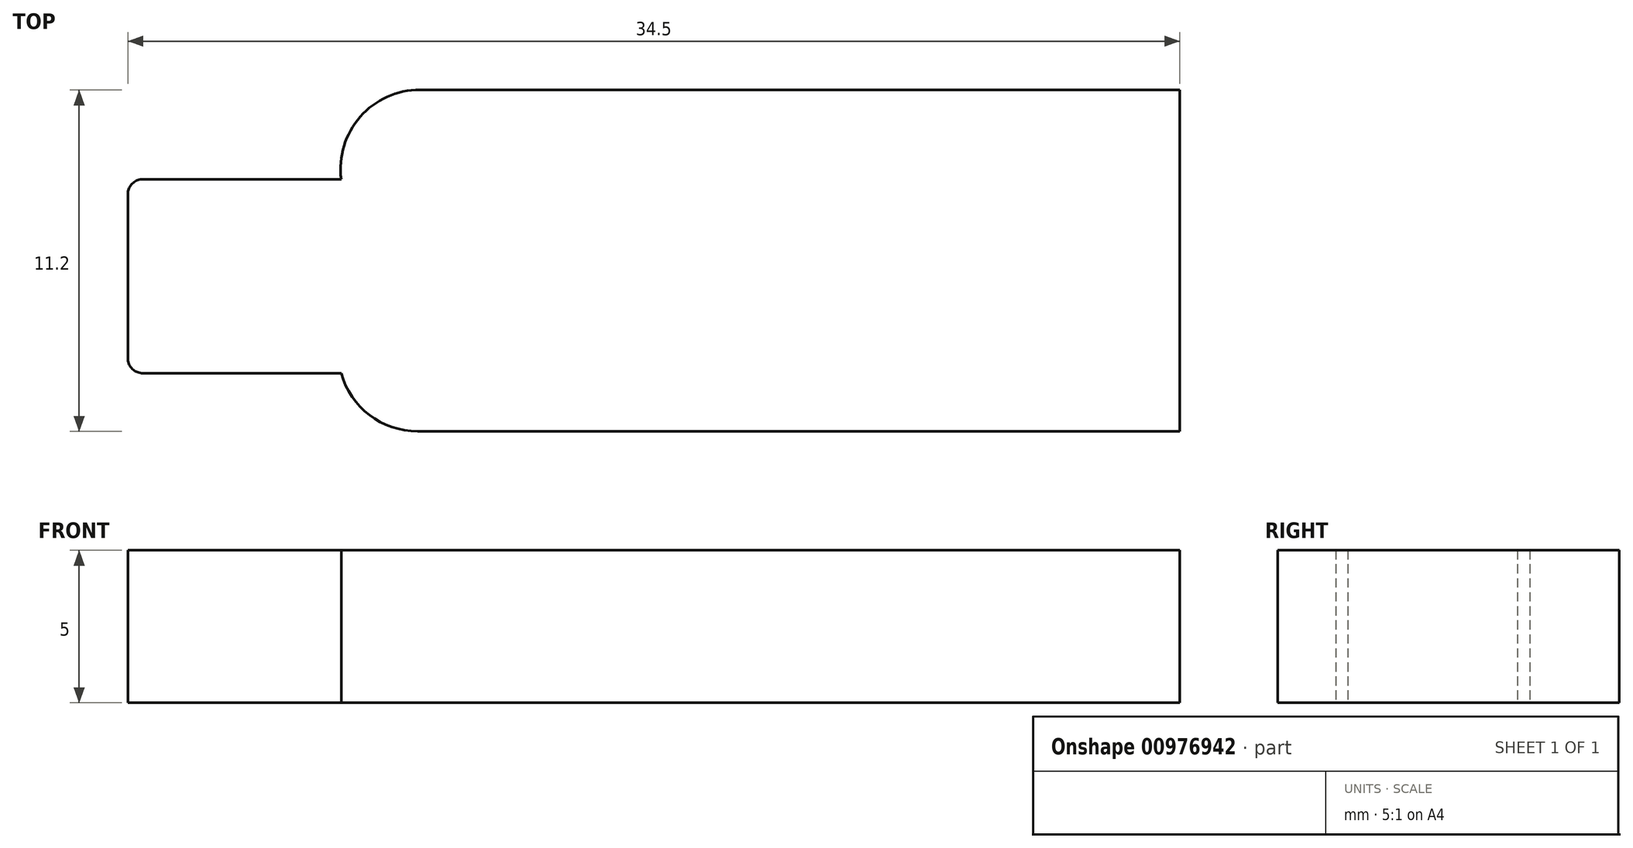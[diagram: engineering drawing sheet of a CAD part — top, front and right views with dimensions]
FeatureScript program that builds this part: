
annotation { "Feature Type Name" : "Feature", "Feature Type Description" : "" }
export const myFeature = defineFeature(function(context is Context, id is Id, definition is map)
    precondition{}
    {
        {
            var Q0;
            Q0=qCreatedBy(makeId("Top.planeOp"),FACE);
            var sketch = newSketch(context, id + "F0", { "sketchPlane" : qUnion([Q0])});
            skLineSegment(sketch, "E0", {"start": v(-13.62, 24.23) * mm, "end": v(11.38, 24.23) * mm});
            skArc(sketch, "E1", {"start": v(-16.13, 26.14) * mm, "mid": v(-15.2, 24.76) * mm, "end": v(-13.62, 24.23) * mm});
            skLineSegment(sketch, "E2", {"start": v(11.38, 24.23) * mm, "end": v(11.38, 35.43) * mm});
            skLineSegment(sketch, "E3", {"start": v(11.38, 35.43) * mm, "end": v(-13.55, 35.43) * mm});
            skArc(sketch, "E4", {"start": v(-13.55, 35.43) * mm, "mid": v(-15.5, 34.55) * mm, "end": v(-16.13, 32.5) * mm});
            skLineSegment(sketch, "E5", {"start": v(-16.13, 32.5) * mm, "end": v(-22.63, 32.5) * mm});
            skLineSegment(sketch, "E6", {"start": v(-16.13, 26.14) * mm, "end": v(-22.63, 26.14) * mm});
            skArc(sketch, "E7", {"start": v(-22.63, 32.5) * mm, "mid": v(-22.94, 32.39) * mm, "end": v(-23.12, 32.1) * mm});
            skArc(sketch, "E8", {"start": v(-23.12, 26.54) * mm, "mid": v(-22.94, 26.25) * mm, "end": v(-22.63, 26.14) * mm});
            skLineSegment(sketch, "E9", {"start": v(-23.12, 32.1) * mm, "end": v(-23.12, 26.54) * mm});
            skLineSegment(sketch, "E10", {"start": v(-16.13, 32.5) * mm, "end": v(-16.13, 26.14) * mm});
            skSolve(sketch);
        }
        {
            var Q0;
            Q0=makeQuery(id+"F0.imprint","IMPRINT",FACE,{"disambiguationData":[TD([[makeQuery(id+"F0.imprint","IMPRINT",EDGE,{"derivedFrom":sQuery(id+"F0.wireOp",EDGE,"E0")}),1.0]])]});
            var Q1;
            Q1=makeQuery(id+"F0.imprint","IMPRINT",FACE,{"disambiguationData":[TD([[makeQuery(id+"F0.imprint","IMPRINT",EDGE,{"derivedFrom":sQuery(id+"F0.wireOp",EDGE,"E5")}),1.0]])]});
            extrude(context, id + "F1", {"entities" : qUnion([Q0, Q1]), "depth" : 5 * mm, "offsetDistance" : 25.4 * mm});
        }
    });
